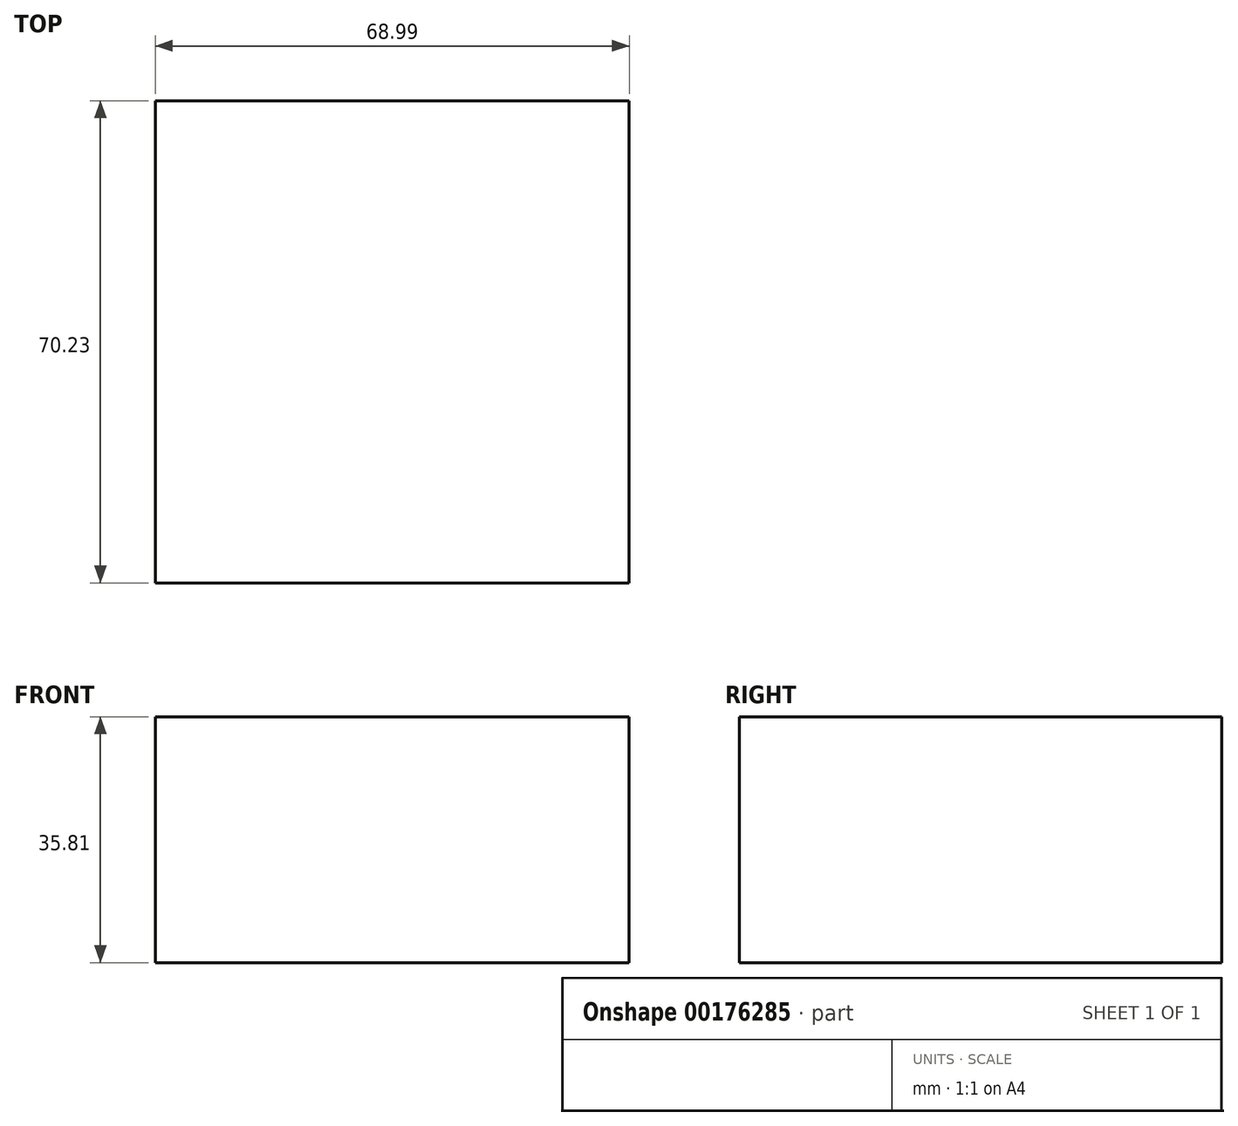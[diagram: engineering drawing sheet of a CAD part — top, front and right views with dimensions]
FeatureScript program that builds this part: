
annotation { "Feature Type Name" : "Feature", "Feature Type Description" : "" }
export const myFeature = defineFeature(function(context is Context, id is Id, definition is map)
    precondition{}
    {
        {
            var Q0;
            Q0=qCreatedBy(makeId("Top.planeOp"),FACE);
            var sketch = newSketch(context, id + "F0", { "sketchPlane" : qUnion([Q0])});
            skLineSegment(sketch, "E0.bottom", {"start": v(-34.92, 32.65) * mm, "end": v(34.07, 32.65) * mm});
            skLineSegment(sketch, "E0.top", {"start": v(-34.92, -37.58) * mm, "end": v(34.07, -37.58) * mm});
            skLineSegment(sketch, "E0.left", {"start": v(-34.92, 32.65) * mm, "end": v(-34.92, -37.58) * mm});
            skLineSegment(sketch, "E0.right", {"start": v(34.07, 32.65) * mm, "end": v(34.07, -37.58) * mm});
            skSolve(sketch);
        }
        {
            var Q0;
            Q0=makeQuery(id+"F0.imprint","IMPRINT",FACE,{"disambiguationData":[TD([[makeQuery(id+"F0.imprint","IMPRINT",EDGE,{"derivedFrom":sQuery(id+"F0.wireOp",EDGE,"E0.bottom")}),-1.0]])]});
            extrude(context, id + "F1", {"entities" : qUnion([Q0]), "depth" : 35.81 * mm});
        }
    });
